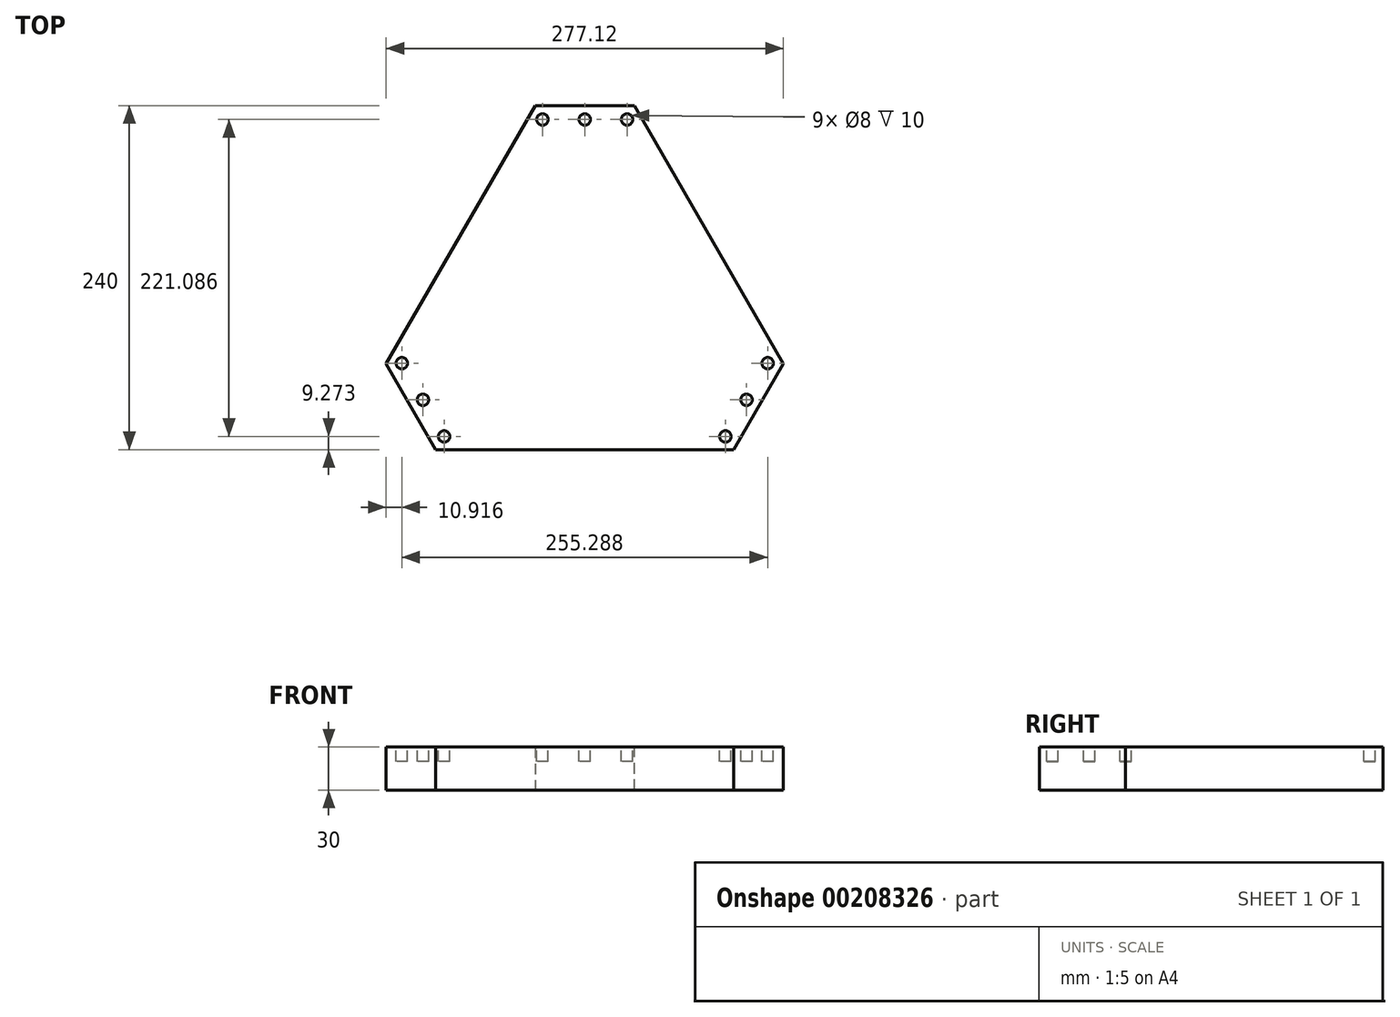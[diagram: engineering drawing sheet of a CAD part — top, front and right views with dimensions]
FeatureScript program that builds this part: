
annotation { "Feature Type Name" : "Feature", "Feature Type Description" : "" }
export const myFeature = defineFeature(function(context is Context, id is Id, definition is map)
    precondition{}
    {
        {
            var Q0;
            Q0=qCreatedBy(makeId("Top.planeOp"),FACE);
            var sketch = newSketch(context, id + "F0", { "sketchPlane" : qUnion([Q0])});
            skCircle(sketch, "E0.cCircle", {"center": v(0, 0) * mm, "radius": 100 * mm, "construction": true});
            skLineSegment(sketch, "E0.0", {"start": v(173.2, -100) * mm, "end": v(-173.2, -100) * mm});
            skLineSegment(sketch, "E0.1", {"start": v(-173.2, -100) * mm, "end": v(0, 200) * mm});
            skLineSegment(sketch, "E0.2", {"start": v(0, 200) * mm, "end": v(173.2, -100) * mm});
            skPoint(sketch, "E0.0.midPoint", {"position": v(0, -100) * mm});
            skSolve(sketch);
        }
        {
            var Q0;
            Q0=qSketchRegion(id+"F0",true);
            extrude(context, id + "F1", {"entities" : qUnion([Q0]), "depth" : 30 * mm});
        }
        {
            var Q0;
            Q0=makeQuery(id+"F1.opExtrude","SWEPT_EDGE",EDGE,{"disambiguationData":[OSD([sQuery(id+"F0.wireOp",EDGE,"E0.0"),sQuery(id+"F0.wireOp",EDGE,"E0.1")])]});
            var Q1;
            Q1=makeQuery(id+"F1.opExtrude","SWEPT_EDGE",EDGE,{"disambiguationData":[OSD([sQuery(id+"F0.wireOp",EDGE,"E0.0"),sQuery(id+"F0.wireOp",EDGE,"E0.2")])]});
            var Q2;
            Q2=makeQuery(id+"F1.opExtrude","SWEPT_EDGE",EDGE,{"disambiguationData":[OSD([sQuery(id+"F0.wireOp",EDGE,"E0.1"),sQuery(id+"F0.wireOp",EDGE,"E0.2")])]});
            chamfer(context, id + "F2", {"entities" : qUnion([Q0, Q1, Q2]), "width" : 40 * mm, "tangentPropagation" : true});
        }
        {
            var Q0;
            Q0=makeQuery(id+"F1.opExtrude","CAP_FACE",FACE,{"disambiguationData":[OSD([sQuery(id+"F0.wireOp",EDGE,"E0.0"),sQuery(id+"F0.wireOp",EDGE,"E0.1"),sQuery(id+"F0.wireOp",EDGE,"E0.2")])],"isStart":false});
            var sketch = newSketch(context, id + "F3", { "sketchPlane" : qUnion([Q0])});
            skLineSegment(sketch, "E1.bottom", {"start": v(-21.5, 108.86) * mm, "end": v(21.5, 108.86) * mm, "construction": true});
            skLineSegment(sketch, "E1.top", {"start": v(-21.5, 151.86) * mm, "end": v(21.5, 151.86) * mm, "construction": true});
            skLineSegment(sketch, "E1.left", {"start": v(-21.5, 108.86) * mm, "end": v(-21.5, 151.86) * mm, "construction": true});
            skLineSegment(sketch, "E1.right", {"start": v(21.5, 108.86) * mm, "end": v(21.5, 151.86) * mm, "construction": true});
            skPoint(sketch, "E1.middle", {"position": v(0, 130.36) * mm});
            skCircle(sketch, "E2", {"center": v(-29.5, 130.36) * mm, "radius": 4 * mm});
            skPoint(sketch, "E2.centerSnap0", {"position": v(-21.5, 130.36) * mm});
            skCircle(sketch, "E3", {"center": v(29.5, 130.36) * mm, "radius": 4 * mm});
            skPoint(sketch, "E3.centerSnap0", {"position": v(21.5, 130.36) * mm});
            skCircle(sketch, "E4.1.0", {"center": v(-98.14, -90.73) * mm, "radius": 4 * mm});
            skCircle(sketch, "E4.1.1", {"center": v(-127.64, -39.63) * mm, "radius": 4 * mm});
            skCircle(sketch, "E4.2.0", {"center": v(127.64, -39.63) * mm, "radius": 4 * mm});
            skCircle(sketch, "E4.2.1", {"center": v(98.14, -90.73) * mm, "radius": 4 * mm});
            skPoint(sketch, "E4.center", {"position": v(0, 0) * mm});
            skCircle(sketch, "E5", {"center": v(0, 130.36) * mm, "radius": 4 * mm});
            skCircle(sketch, "E6.1.0", {"center": v(-112.9, -65.18) * mm, "radius": 4 * mm});
            skCircle(sketch, "E6.2.0", {"center": v(112.9, -65.18) * mm, "radius": 4 * mm});
            skSolve(sketch);
        }
        {
            var Q0;
            Q0=qSketchRegion(id+"F3",true);
            extrude(context, id + "F4", {"entities" : qUnion([Q0]), "operationType" : NewBodyOperationType.REMOVE, "oppositeDirection" : true, "depth" : 10 * mm});
        }
    });
